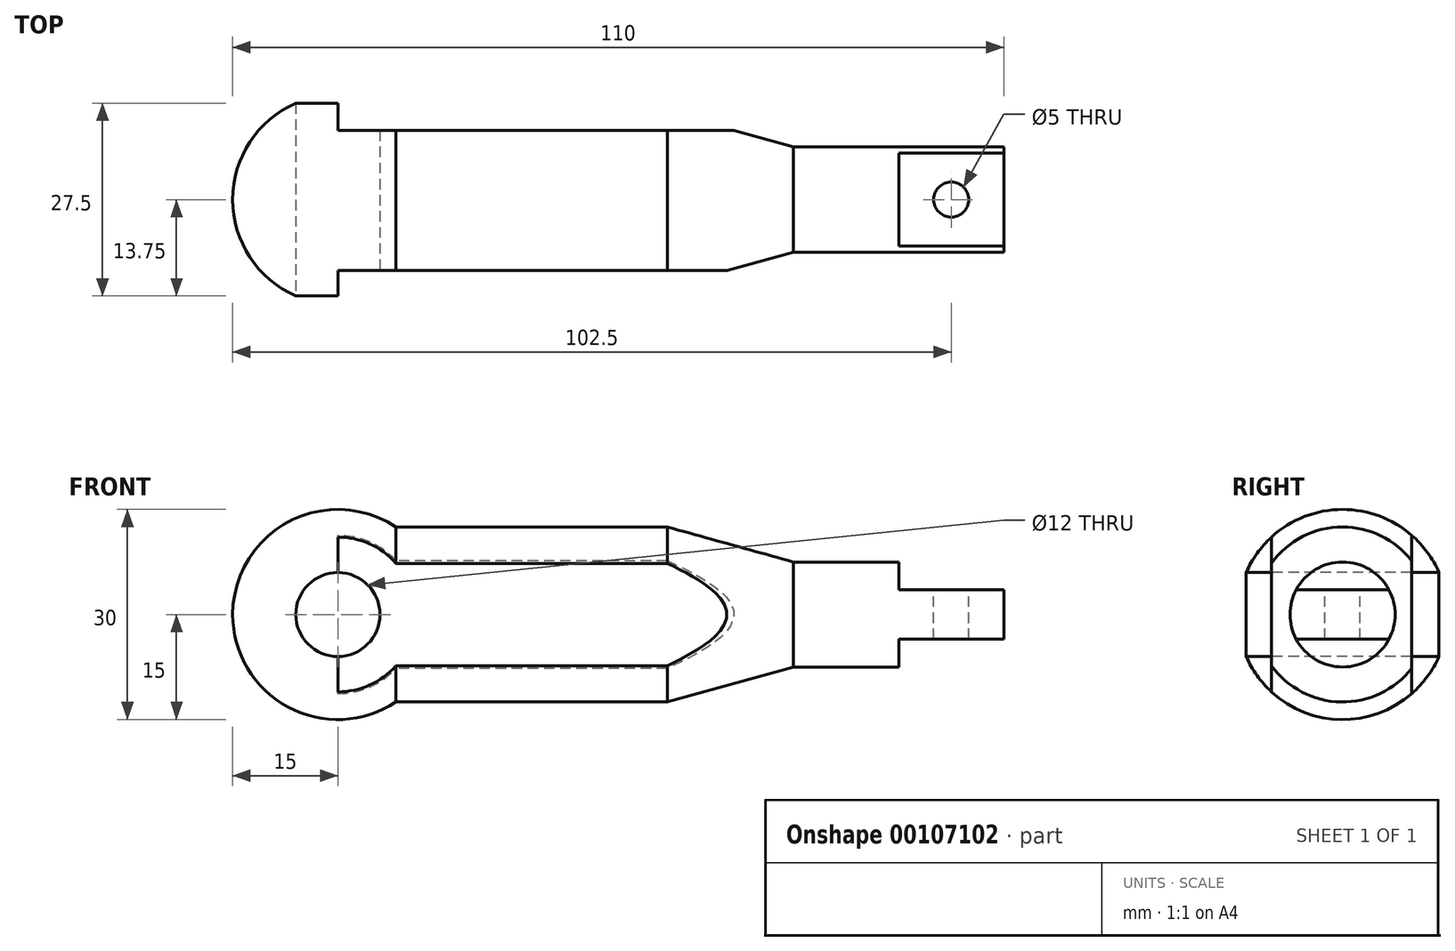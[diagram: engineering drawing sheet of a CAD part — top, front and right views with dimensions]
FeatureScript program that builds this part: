
annotation { "Feature Type Name" : "Feature", "Feature Type Description" : "" }
export const myFeature = defineFeature(function(context is Context, id is Id, definition is map)
    precondition{}
    {
        {
            var Q0;
            Q0=qCreatedBy(makeId("Front.planeOp"),FACE);
            var sketch = newSketch(context, id + "F0", { "sketchPlane" : qUnion([Q0])});
            skLineSegment(sketch, "E0", {"start": v(95, 7.5) * mm, "end": v(65, 7.5) * mm});
            skLineSegment(sketch, "E1", {"start": v(65, 7.5) * mm, "end": v(47, 12.5) * mm});
            skLineSegment(sketch, "E2", {"start": v(47, 12.5) * mm, "end": v(8.3, 12.5) * mm});
            skArc(sketch, "E3", {"start": v(8.3, 12.5) * mm, "mid": v(-7.1, 13.22) * mm, "end": v(-15, 0) * mm});
            skLineSegment(sketch, "E4", {"start": v(-15, 0) * mm, "end": v(95, 0) * mm});
            skLineSegment(sketch, "E5", {"start": v(-31.88, 0) * mm, "end": v(156.93, 0) * mm, "construction": true});
            skLineSegment(sketch, "E6", {"start": v(95, 7.5) * mm, "end": v(95, 0) * mm});
            skSolve(sketch);
        }
        {
            var Q0;
            Q0 = qSketchRegion(id + "F0", true);
            var Q1;
            Q1=sQuery(id+"F0.wireOp",EDGE,"E5");
            revolve(context, id + "F1", {"entities" : qUnion([Q0]), "axis" : qUnion([Q1]), "revolveType" : RevolveType.FULL});
        }
        {
            var Q0;
            Q0=qCreatedBy(makeId("Front.planeOp"),FACE);
            var sketch = newSketch(context, id + "F2", { "sketchPlane" : qUnion([Q0])});
            skCircle(sketch, "E7", {"center": v(0, 0) * mm, "radius": 6 * mm});
            skSolve(sketch);
        }
        {
            var Q0;
            Q0 = qSketchRegion(id + "F2", true);
            extrude(context, id + "F3", {"entities" : qUnion([Q0]), "operationType" : NewBodyOperationType.REMOVE, "endBound" : BoundingType.THROUGH_ALL, "oppositeDirection" : true, "depth" : 25 * mm});
        }
        {
            var Q0;
            Q0=makeQuery(id+"F3.boolean.opBoolean","COPY",FACE,{"derivedFrom":makeQuery(id+"F3.opExtrude","CAP_FACE",FACE,{"disambiguationData":[OSD([sQuery(id+"F2.wireOp",EDGE,"E7")])],"isStart":true})});
            extrude(context, id + "F4", {"entities" : qUnion([Q0]), "operationType" : NewBodyOperationType.REMOVE, "oppositeDirection" : true, "depth" : 25 * mm});
        }
        {
            var Q0;
            Q0=qCreatedBy(makeId("Right.planeOp"),FACE);
            var sketch = newSketch(context, id + "F5", { "sketchPlane" : qUnion([Q0])});
            skLineSegment(sketch, "E8.left", {"start": v(9.86, 13.46) * mm, "end": v(9.86, -16) * mm});
            skLineSegment(sketch, "E8.right", {"start": v(-10.14, 13.46) * mm, "end": v(-10.14, -16) * mm});
            skLineSegment(sketch, "E9", {"start": v(-10.14, 13.46) * mm, "end": v(-15.78, 13.46) * mm});
            skLineSegment(sketch, "E10", {"start": v(-15.78, 13.46) * mm, "end": v(-15.78, -16) * mm});
            skLineSegment(sketch, "E11", {"start": v(-15.78, -16) * mm, "end": v(-10.14, -16) * mm});
            skLineSegment(sketch, "E12.bottom", {"start": v(9.86, -16) * mm, "end": v(9.86, -16) * mm});
            skLineSegment(sketch, "E12.top", {"start": v(9.86, 13.46) * mm, "end": v(9.86, 13.46) * mm});
            skLineSegment(sketch, "E12.left", {"start": v(9.86, -16) * mm, "end": v(9.86, 13.46) * mm});
            skLineSegment(sketch, "E12.right", {"start": v(9.86, -16) * mm, "end": v(9.86, 13.46) * mm});
            skLineSegment(sketch, "E13.bottom", {"start": v(9.86, 13.46) * mm, "end": v(15.5, 13.46) * mm});
            skLineSegment(sketch, "E13.top", {"start": v(9.86, -16.19) * mm, "end": v(15.5, -16.19) * mm});
            skLineSegment(sketch, "E13.left", {"start": v(9.86, 13.46) * mm, "end": v(9.86, -16.19) * mm});
            skLineSegment(sketch, "E13.right", {"start": v(15.5, 13.46) * mm, "end": v(15.5, -16.19) * mm});
            skSolve(sketch);
        }
        {
            var Q0;
            Q0 = qSketchRegion(id + "F5", true);
            extrude(context, id + "F6", {"entities" : qUnion([Q0]), "operationType" : NewBodyOperationType.REMOVE, "depth" : 110 * mm});
        }
        {
            var Q0;
            Q0=makeQuery(id+"F1.opRevolve","SWEPT_FACE",FACE,{"disambiguationData":[OSD([sQuery(id+"F0.wireOp",EDGE,"E6")])]});
            var sketch = newSketch(context, id + "F8", { "sketchPlane" : qUnion([Q0])});
            skLineSegment(sketch, "E14", {"start": v(0, 3.5) * mm, "end": v(12.56, 3.5) * mm});
            skLineSegment(sketch, "E15", {"start": v(12.56, -3.5) * mm, "end": v(0, -3.5) * mm});
            skLineSegment(sketch, "E16.bottom", {"start": v(12.56, 3.5) * mm, "end": v(-19.75, 3.5) * mm});
            skLineSegment(sketch, "E16.top", {"start": v(12.56, 8.6) * mm, "end": v(-19.75, 8.6) * mm});
            skLineSegment(sketch, "E16.left", {"start": v(12.56, 3.5) * mm, "end": v(12.56, 8.6) * mm});
            skLineSegment(sketch, "E16.right", {"start": v(-19.75, 3.5) * mm, "end": v(-19.75, 8.6) * mm});
            skLineSegment(sketch, "E17.bottom", {"start": v(12.56, -3.5) * mm, "end": v(-19.95, -3.5) * mm});
            skLineSegment(sketch, "E17.top", {"start": v(12.56, -9.28) * mm, "end": v(-19.95, -9.28) * mm});
            skLineSegment(sketch, "E17.left", {"start": v(12.56, -3.5) * mm, "end": v(12.56, -9.28) * mm});
            skLineSegment(sketch, "E17.right", {"start": v(-19.95, -3.5) * mm, "end": v(-19.95, -9.28) * mm});
            skSolve(sketch);
        }
        {
            var Q0;
            Q0 = qSketchRegion(id + "F8", true);
            extrude(context, id + "F9", {"entities" : qUnion([Q0]), "operationType" : NewBodyOperationType.REMOVE, "oppositeDirection" : true, "depth" : 15 * mm});
        }
        {
            var Q0;
            Q0=makeQuery(id+"F9.boolean.opBoolean","COPY",FACE,{"derivedFrom":makeQuery(id+"F9.opExtrude","SWEPT_FACE",FACE,{"disambiguationData":[OSD([sQuery(id+"F8.wireOp",EDGE,"E16.bottom")])]})});
            var sketch = newSketch(context, id + "F10", { "sketchPlane" : qUnion([Q0])});
            skCircle(sketch, "E18", {"center": v(87.5, 0) * mm, "radius": 2.5 * mm});
            skPoint(sketch, "E18.centerSnap0", {"position": v(80, 0) * mm});
            skSolve(sketch);
        }
        {
            var Q0;
            Q0 = qSketchRegion(id + "F10", true);
            extrude(context, id + "F11", {"entities" : qUnion([Q0]), "operationType" : NewBodyOperationType.REMOVE, "endBound" : BoundingType.THROUGH_ALL, "oppositeDirection" : true, "depth" : 25 * mm});
        }
    });
